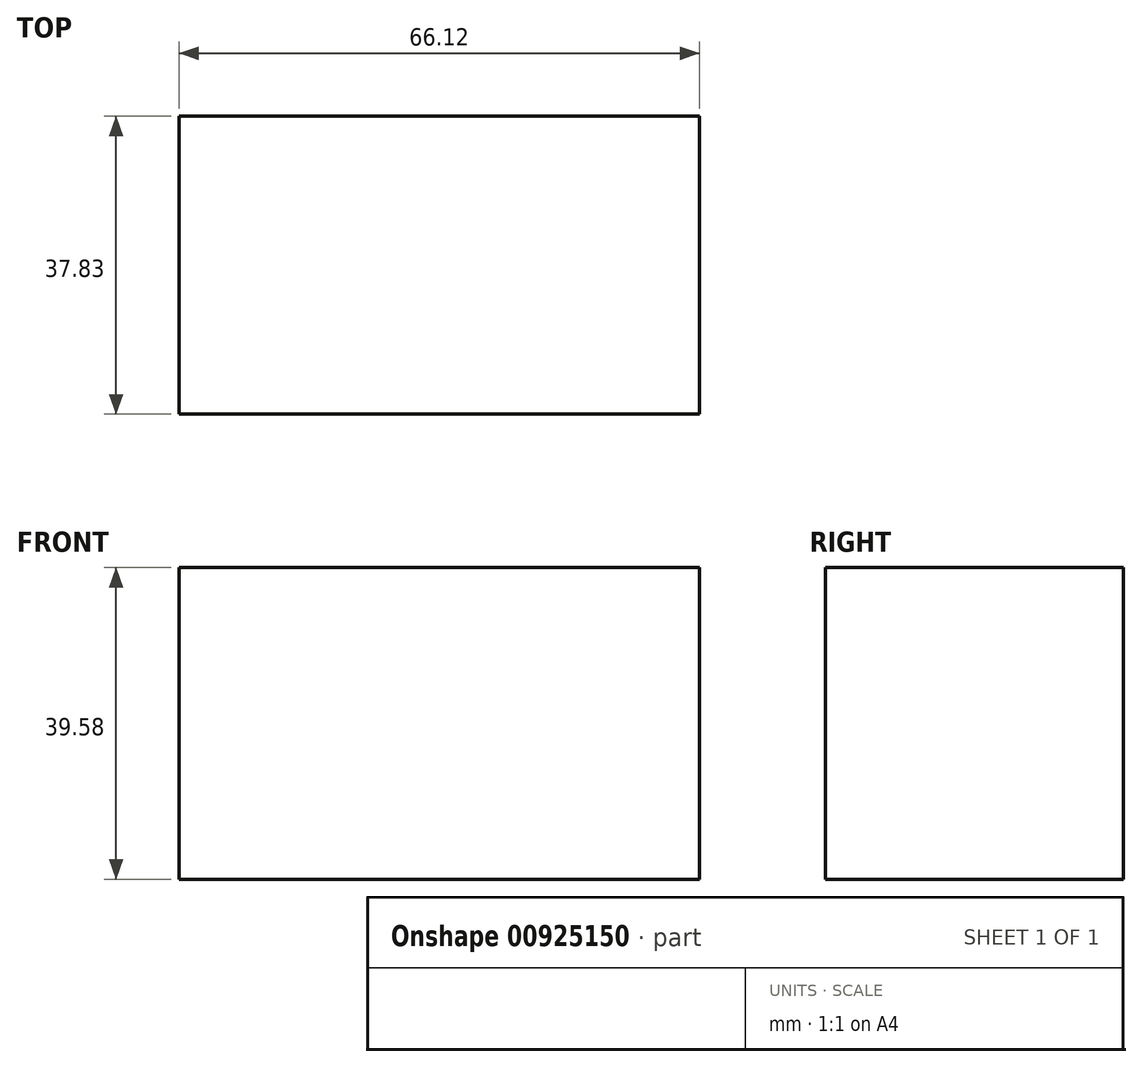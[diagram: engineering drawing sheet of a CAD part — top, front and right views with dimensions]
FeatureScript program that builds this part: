
annotation { "Feature Type Name" : "Feature", "Feature Type Description" : "" }
export const myFeature = defineFeature(function(context is Context, id is Id, definition is map)
    precondition{}
    {
        {
            var Q0;
            Q0=qCreatedBy(makeId("Front.planeOp"),FACE);
            var sketch = newSketch(context, id + "F0", { "sketchPlane" : qUnion([Q0])});
            skLineSegment(sketch, "E0.bottom", {"start": v(33.06, -19.79) * mm, "end": v(-33.06, -19.79) * mm});
            skLineSegment(sketch, "E0.top", {"start": v(33.06, 19.79) * mm, "end": v(-33.06, 19.79) * mm});
            skLineSegment(sketch, "E0.left", {"start": v(33.06, -19.79) * mm, "end": v(33.06, 19.79) * mm});
            skLineSegment(sketch, "E0.right", {"start": v(-33.06, -19.79) * mm, "end": v(-33.06, 19.79) * mm});
            skPoint(sketch, "E0.middle", {"position": v(0, 0) * mm});
            skArc(sketch, "E1", {"start": v(-9.54, 14.29) * mm, "mid": v(-13.26, 51.43) * mm, "end": v(-33.06, 19.79) * mm});
            skArc(sketch, "E2", {"start": v(1.18, 26.67) * mm, "mid": v(-0.29, 23.05) * mm, "end": v(-2.44, 19.79) * mm});
            skSolve(sketch);
        }
        {
            var Q0;
            Q0=makeQuery(id+"F0.imprint","IMPRINT",FACE,{"disambiguationData":[TD([[makeQuery(id+"F0.imprint","IMPRINT",EDGE,{"derivedFrom":sQuery(id+"F0.wireOp",EDGE,"E0.bottom")}),-1.0]])]});
            extrude(context, id + "F1", {"entities" : qUnion([Q0]), "depth" : 37.83 * mm, "offsetDistance" : 25 * mm});
        }
    });
